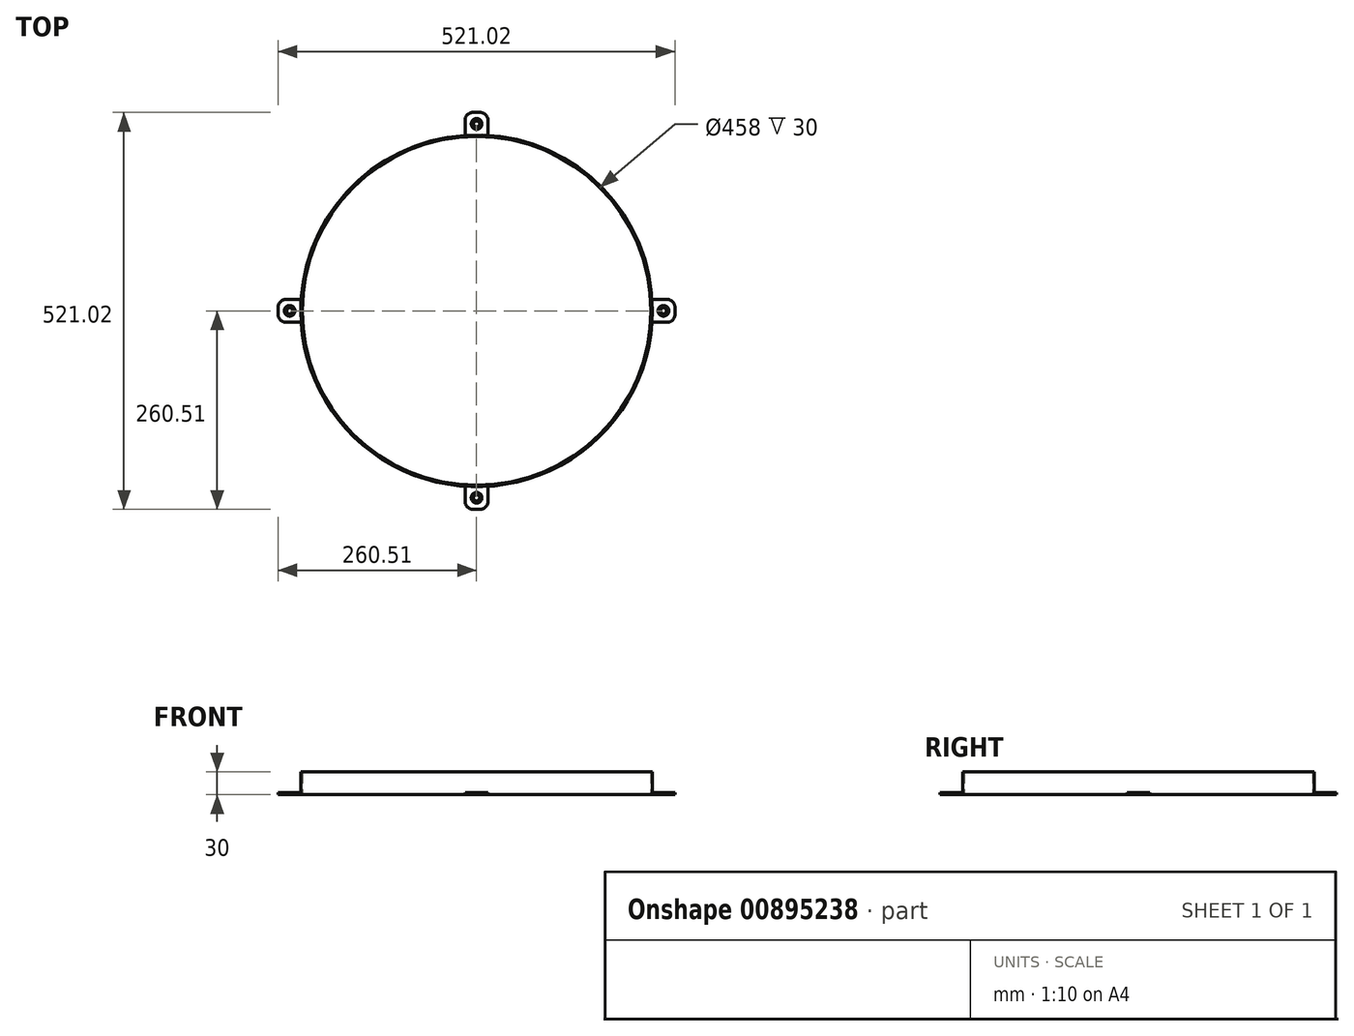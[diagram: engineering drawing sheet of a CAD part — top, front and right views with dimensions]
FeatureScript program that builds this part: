
annotation { "Feature Type Name" : "Feature", "Feature Type Description" : "" }
export const myFeature = defineFeature(function(context is Context, id is Id, definition is map)
    precondition{}
    {
        {
            var Q0;
            Q0=qCreatedBy(makeId("Top.planeOp"),FACE);
            var sketch = newSketch(context, id + "F0", { "sketchPlane" : qUnion([Q0])});
            skCircle(sketch, "E0", {"center": v(0, 0) * mm, "radius": 231 * mm});
            skCircle(sketch, "E1", {"center": v(0, 0) * mm, "radius": 229 * mm});
            skSolve(sketch);
        }
        {
            var Q0;
            Q0 = qSketchRegion(id + "F0", true);
            extrude(context, id + "F1", {"entities" : qUnion([Q0]), "depth" : 30 * mm, "offsetDistance" : 25 * mm});
        }
        {
            var Q0;
            {var subQ0=makeQuery(id+"FOfs6LXXoXaqfb5_1.boolean.opBoolean","MERGE",FACE,{"derivedFrom":[makeQuery(id+"F1.opExtrude","CAP_FACE",FACE,{"disambiguationData":[OSD([sQuery(id+"F0.wireOp",EDGE,"E0"),sQuery(id+"F0.wireOp",EDGE,"E1")])],"isStart":true}),makeQuery(id+"FOfs6LXXoXaqfb5_1.opExtrude","CAP_FACE",FACE,{"disambiguationData":[OSD([sQuery(id+"Fq126zPfvdtfzcJ_1.wireOp",EDGE,"aM8YIA2p-sepS-RrJB-uuBs-LwZfDOID8hhf.bottom"),sQuery(id+"Fq126zPfvdtfzcJ_1.wireOp",EDGE,"aM8YIA2p-sepS-RrJB-uuBs-LwZfDOID8hhf.top"),sQuery(id+"Fq126zPfvdtfzcJ_1.wireOp",EDGE,"aM8YIA2p-sepS-RrJB-uuBs-LwZfDOID8hhf.left"),sQuery(id+"Fq126zPfvdtfzcJ_1.wireOp",EDGE,"HM3TmMY7-uQYK-AxsU-DERO-EDIUWc1xLfHu")])],"isStart":false})]});Q0=makeQuery(id+"F8.boolean.opBoolean","MERGE",FACE,{"derivedFrom":[subQ0,makeQuery(id+"F8.opPattern","COPY",FACE,{"derivedFrom":subQ0,"instanceName":"1"}),makeQuery(id+"F8.opPattern","COPY",FACE,{"derivedFrom":subQ0,"instanceName":"2"}),makeQuery(id+"F8.opPattern","COPY",FACE,{"derivedFrom":subQ0,"instanceName":"3"}),makeQuery(id+"F8.opPattern","COPY",FACE,{"derivedFrom":subQ0,"instanceName":"4"}),makeQuery(id+"F8.opPattern","COPY",FACE,{"derivedFrom":subQ0,"instanceName":"5"})]});}
            var sketch = newSketch(context, id + "F2", { "sketchPlane" : qUnion([Q0])});
            skLineSegment(sketch, "E2.bottom", {"start": v(-15, -230.51) * mm, "end": v(15, -230.51) * mm});
            skLineSegment(sketch, "E2.top", {"start": v(-15, -260.51) * mm, "end": v(15, -260.51) * mm});
            skLineSegment(sketch, "E2.left", {"start": v(-15, -230.51) * mm, "end": v(-15, -260.51) * mm});
            skLineSegment(sketch, "E2.right", {"start": v(15, -230.51) * mm, "end": v(15, -260.51) * mm});
            skSolve(sketch);
        }
        {
            var Q0;
            Q0 = qSketchRegion(id + "F2", true);
            extrude(context, id + "F3", {"entities" : qUnion([Q0]), "operationType" : NewBodyOperationType.ADD, "oppositeDirection" : true, "depth" : 3 * mm, "offsetDistance" : 25 * mm});
        }
        {
            var Q0;
            {var subQ0=makeQuery(id+"F3.boolean.opBoolean","MERGE",FACE,{"derivedFrom":[makeQuery(id+"F1.opExtrude","CAP_FACE",FACE,{"disambiguationData":[OSD([sQuery(id+"F0.wireOp",EDGE,"E0"),sQuery(id+"F0.wireOp",EDGE,"E1")])],"isStart":true}),makeQuery(id+"F3.opExtrude","CAP_FACE",FACE,{"disambiguationData":[OSD([sQuery(id+"F2.wireOp",EDGE,"E2.bottom"),sQuery(id+"F2.wireOp",EDGE,"E2.top"),sQuery(id+"F2.wireOp",EDGE,"E2.left"),sQuery(id+"F2.wireOp",EDGE,"E2.right")])],"isStart":true})]});Q0=makeQuery(id+"F8.boolean.opBoolean","MERGE",FACE,{"derivedFrom":[subQ0,makeQuery(id+"F8.opPattern","COPY",FACE,{"derivedFrom":subQ0,"instanceName":"1"}),makeQuery(id+"F8.opPattern","COPY",FACE,{"derivedFrom":subQ0,"instanceName":"2"}),makeQuery(id+"F8.opPattern","COPY",FACE,{"derivedFrom":subQ0,"instanceName":"3"}),makeQuery(id+"F8.opPattern","COPY",FACE,{"derivedFrom":subQ0,"instanceName":"4"}),makeQuery(id+"F8.opPattern","COPY",FACE,{"derivedFrom":subQ0,"instanceName":"5"})]});}
            var sketch = newSketch(context, id + "F4", { "sketchPlane" : qUnion([Q0])});
            skCircle(sketch, "E3", {"center": v(0, -245.51) * mm, "radius": 4 * mm});
            skPoint(sketch, "E3.centerSnap0", {"position": v(0, -260.51) * mm});
            skPoint(sketch, "E3.centerSnap1", {"position": v(-15, -245.51) * mm});
            skSolve(sketch);
        }
        {
            var Q0;
            Q0 = qSketchRegion(id + "F4", true);
            extrude(context, id + "F5", {"entities" : qUnion([Q0]), "operationType" : NewBodyOperationType.REMOVE, "oppositeDirection" : true, "depth" : 25 * mm, "offsetDistance" : 25 * mm});
        }
        {
            var Q0;
            Q0=makeQuery(id+"F3.opExtrude","SWEPT_EDGE",EDGE,{"disambiguationData":[OSD([sQuery(id+"F2.wireOp",EDGE,"E2.top"),sQuery(id+"F2.wireOp",EDGE,"E2.left")])]});
            var Q1;
            Q1=makeQuery(id+"F3.opExtrude","SWEPT_EDGE",EDGE,{"disambiguationData":[OSD([sQuery(id+"F2.wireOp",EDGE,"E2.top"),sQuery(id+"F2.wireOp",EDGE,"E2.right")])]});
            fillet(context, id + "F6", {"entities" : qUnion([Q0, Q1]), "radius" : 10 * mm, "tangentPropagation" : true, "allowEdgeOverflow" : false});
        }
        {
            var Q0;
            Q0=qCreatedBy(makeId("Right.planeOp"),FACE);
            var sketch = newSketch(context, id + "F7", { "sketchPlane" : qUnion([Q0])});
            skLineSegment(sketch, "E4", {"start": v(0, 0) * mm, "end": v(0, -102.23) * mm});
            skSolve(sketch);
        }
        {
            var Q0;
            Q0=makeQuery(id+"F1.opExtrude","SWEPT_BODY",BODY,{"disambiguationData":[OSD([sQuery(id+"F0.wireOp",EDGE,"E0"),sQuery(id+"F0.wireOp",EDGE,"E1")])]});
            var Q1;
            Q1=sQuery(id+"F7.wireOp",EDGE,"E4");
            circularPattern(context, id + "F8", {"operationType" : NewBodyOperationType.ADD, "entities" : qUnion([Q0]), "axis" : qUnion([Q1]), "angle" : 360 * degree, "instanceCount" : 4, "equalSpace" : true});
        }
        {
            var Q0;
            Q0=makeQuery(id+"F8.opPattern","COPY",EDGE,{"derivedFrom":makeQuery(id+"F5.boolean.opBoolean","INTERSECT",EDGE,{"derivedFrom":[makeQuery(id+"F3.opExtrude","CAP_FACE",FACE,{"disambiguationData":[OSD([sQuery(id+"F2.wireOp",EDGE,"E2.bottom"),sQuery(id+"F2.wireOp",EDGE,"E2.top"),sQuery(id+"F2.wireOp",EDGE,"E2.left"),sQuery(id+"F2.wireOp",EDGE,"E2.right")])],"isStart":false}),makeQuery(id+"F5.opExtrude","SWEPT_FACE",FACE,{"disambiguationData":[OSD([sQuery(id+"F4.wireOp",EDGE,"E3")])]})]}),"instanceName":"3"});
            var Q1;
            Q1=makeQuery(id+"F5.boolean.opBoolean","INTERSECT",EDGE,{"derivedFrom":[makeQuery(id+"F3.opExtrude","CAP_FACE",FACE,{"disambiguationData":[OSD([sQuery(id+"F2.wireOp",EDGE,"E2.bottom"),sQuery(id+"F2.wireOp",EDGE,"E2.top"),sQuery(id+"F2.wireOp",EDGE,"E2.left"),sQuery(id+"F2.wireOp",EDGE,"E2.right")])],"isStart":false}),makeQuery(id+"F5.opExtrude","SWEPT_FACE",FACE,{"disambiguationData":[OSD([sQuery(id+"F4.wireOp",EDGE,"E3")])]})]});
            var Q2;
            Q2=makeQuery(id+"F8.opPattern","COPY",EDGE,{"derivedFrom":makeQuery(id+"F5.boolean.opBoolean","INTERSECT",EDGE,{"derivedFrom":[makeQuery(id+"F3.opExtrude","CAP_FACE",FACE,{"disambiguationData":[OSD([sQuery(id+"F2.wireOp",EDGE,"E2.bottom"),sQuery(id+"F2.wireOp",EDGE,"E2.top"),sQuery(id+"F2.wireOp",EDGE,"E2.left"),sQuery(id+"F2.wireOp",EDGE,"E2.right")])],"isStart":false}),makeQuery(id+"F5.opExtrude","SWEPT_FACE",FACE,{"disambiguationData":[OSD([sQuery(id+"F4.wireOp",EDGE,"E3")])]})]}),"instanceName":"1"});
            var Q3;
            Q3=makeQuery(id+"F8.opPattern","COPY",EDGE,{"derivedFrom":makeQuery(id+"F5.boolean.opBoolean","INTERSECT",EDGE,{"derivedFrom":[makeQuery(id+"F3.opExtrude","CAP_FACE",FACE,{"disambiguationData":[OSD([sQuery(id+"F2.wireOp",EDGE,"E2.bottom"),sQuery(id+"F2.wireOp",EDGE,"E2.top"),sQuery(id+"F2.wireOp",EDGE,"E2.left"),sQuery(id+"F2.wireOp",EDGE,"E2.right")])],"isStart":false}),makeQuery(id+"F5.opExtrude","SWEPT_FACE",FACE,{"disambiguationData":[OSD([sQuery(id+"F4.wireOp",EDGE,"E3")])]})]}),"instanceName":"2"});
            chamfer(context, id + "F9", {"entities" : qUnion([Q0, Q1, Q2, Q3]), "width" : 3 * mm, "tangentPropagation" : true});
        }
    });
